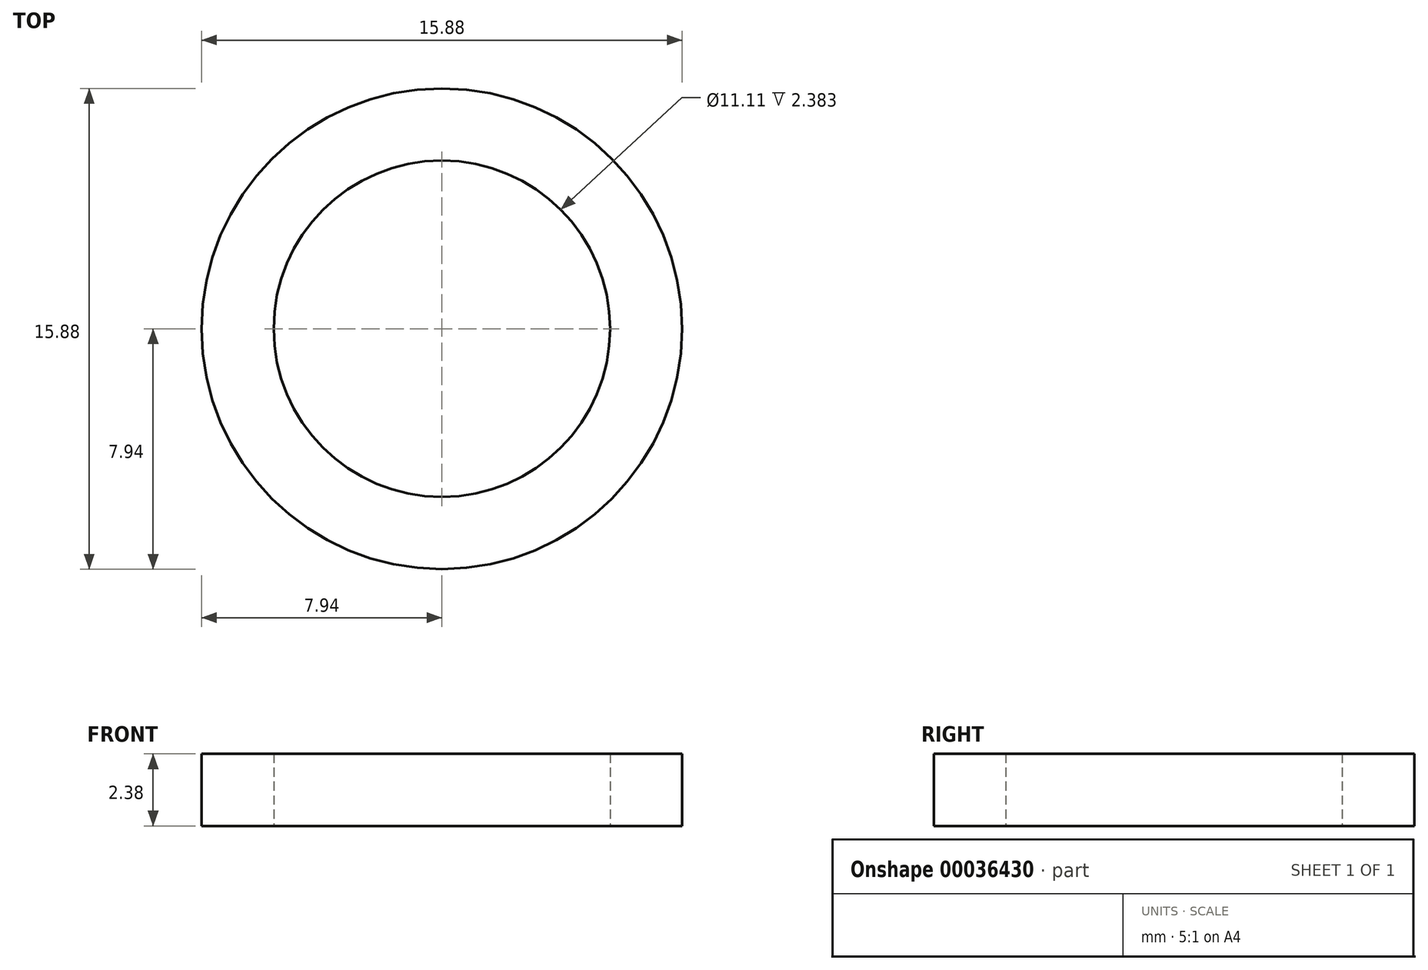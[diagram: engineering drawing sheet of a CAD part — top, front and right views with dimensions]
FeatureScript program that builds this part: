
annotation { "Feature Type Name" : "Feature", "Feature Type Description" : "" }
export const myFeature = defineFeature(function(context is Context, id is Id, definition is map)
    precondition{}
    {
        {
            var Q0;
            Q0=qCreatedBy(makeId("Top.planeOp"),FACE);
            var sketch = newSketch(context, id + "F0", { "sketchPlane" : qUnion([Q0])});
            skCircle(sketch, "E0", {"center": v(0, 0) * mm, "radius": 7.94 * mm});
            skCircle(sketch, "E1", {"center": v(0, 0) * mm, "radius": 5.56 * mm});
            skSolve(sketch);
        }
        {
            var Q0;
            Q0=makeQuery(id+"F0.imprint","IMPRINT",FACE,{"disambiguationData":[TD([[makeQuery(id+"F0.imprint","IMPRINT",EDGE,{"derivedFrom":sQuery(id+"F0.wireOp",EDGE,"E0")}),1.0]])]});
            extrude(context, id + "F1", {"entities" : qUnion([Q0]), "depth" : 2.38 * mm});
        }
    });
